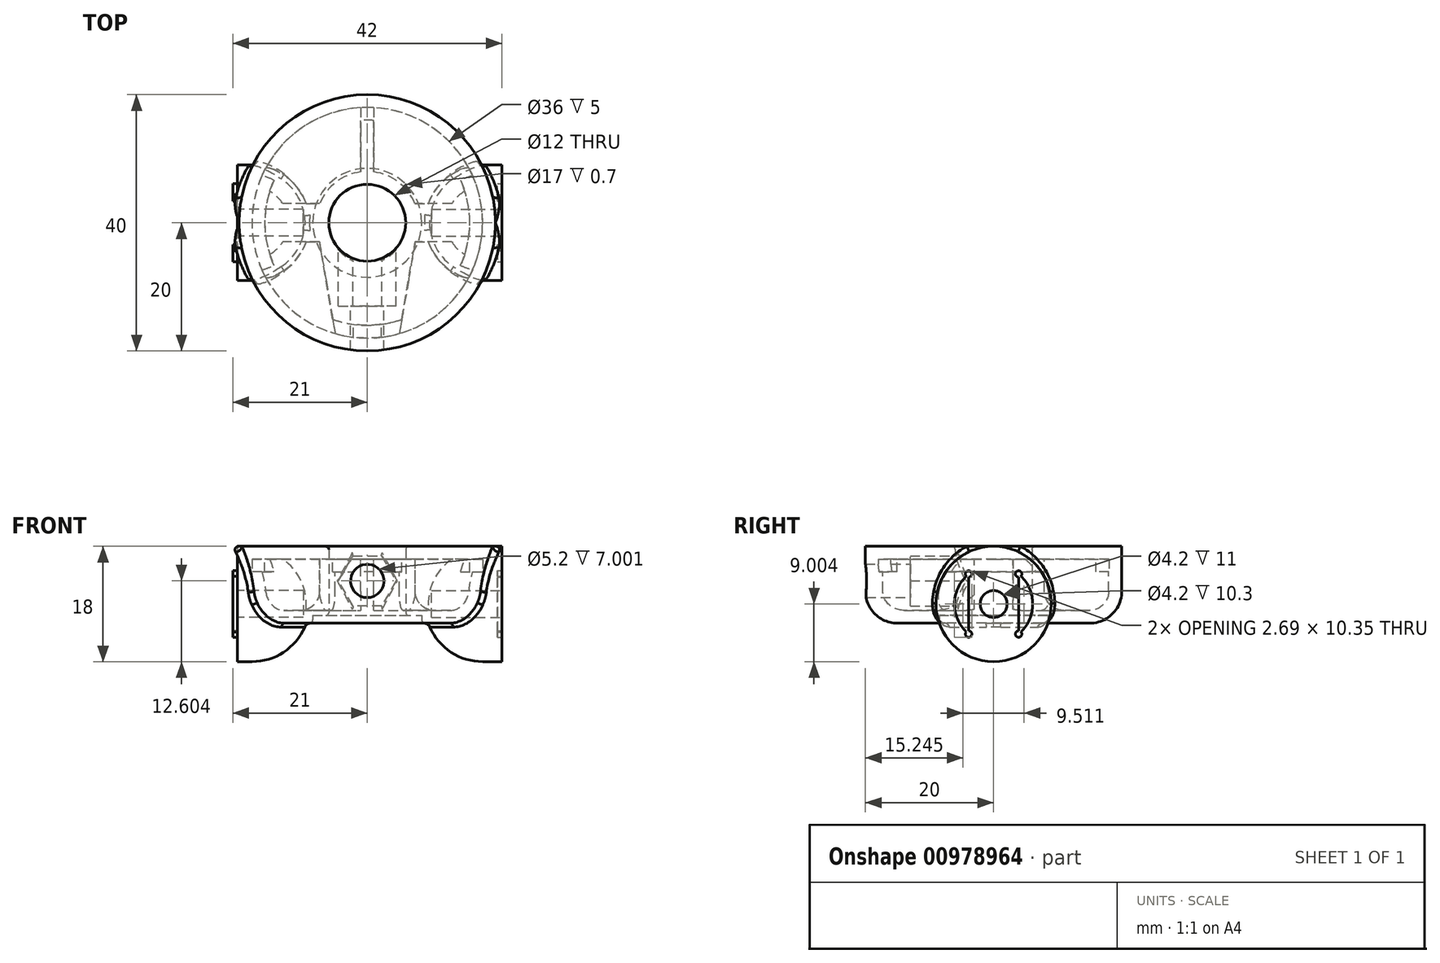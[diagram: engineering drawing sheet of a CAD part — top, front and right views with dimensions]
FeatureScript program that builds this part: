
annotation { "Feature Type Name" : "Feature", "Feature Type Description" : "" }
export const myFeature = defineFeature(function(context is Context, id is Id, definition is map)
    precondition{}
    {
        {
            var Q0;
            Q0=qCreatedBy(makeId("Front.planeOp"),FACE);
            var sketch = newSketch(context, id + "F0", { "sketchPlane" : qUnion([Q0])});
            skLineSegment(sketch, "E0", {"start": v(0, 0) * mm, "end": v(0, 29.29) * mm, "construction": true});
            skLineSegment(sketch, "E1", {"start": v(-6, 15.66) * mm, "end": v(-6, 4.86) * mm});
            skLineSegment(sketch, "E2", {"start": v(-6, 4.86) * mm, "end": v(-8.5, 4.86) * mm});
            skLineSegment(sketch, "E3", {"start": v(-8.5, 4.86) * mm, "end": v(-8.5, 3.66) * mm});
            skLineSegment(sketch, "E4", {"start": v(-8.5, 3.66) * mm, "end": v(-8.5, 3.66) * mm});
            skLineSegment(sketch, "E5", {"start": v(-8.5, 3.66) * mm, "end": v(-15, 3.66) * mm});
            skLineSegment(sketch, "E6", {"start": v(-20, 8.66) * mm, "end": v(-20, 15.66) * mm});
            skLineSegment(sketch, "E7", {"start": v(-20, 15.66) * mm, "end": v(-18, 15.66) * mm});
            skLineSegment(sketch, "E8", {"start": v(-18, 15.66) * mm, "end": v(-18, 15.66) * mm});
            skLineSegment(sketch, "E9", {"start": v(-18, 15.66) * mm, "end": v(-18, 8.66) * mm});
            skLineSegment(sketch, "E10", {"start": v(-15, 5.66) * mm, "end": v(-11, 5.66) * mm});
            skLineSegment(sketch, "E11", {"start": v(-8, 5.66) * mm, "end": v(-8, 5.66) * mm});
            skLineSegment(sketch, "E12", {"start": v(-8, 8.66) * mm, "end": v(-8, 15.66) * mm});
            skLineSegment(sketch, "E13", {"start": v(-6, 15.66) * mm, "end": v(-8, 15.66) * mm});
            skPoint(sketch, "E14.visualSharp", {"position": v(-20, 3.66) * mm});
            skArc(sketch, "E14.filletArc", {"start": v(-20, 8.66) * mm, "mid": v(-18.54, 5.13) * mm, "end": v(-15, 3.66) * mm});
            skPoint(sketch, "E15.visualSharp", {"position": v(-18, 5.66) * mm});
            skArc(sketch, "E15.filletArc", {"start": v(-18, 8.66) * mm, "mid": v(-17.12, 6.54) * mm, "end": v(-15, 5.66) * mm});
            skPoint(sketch, "E16.visualSharp", {"position": v(-8, 5.66) * mm});
            skArc(sketch, "E16.filletArc", {"start": v(-11, 5.66) * mm, "mid": v(-8.88, 6.54) * mm, "end": v(-8, 8.66) * mm});
            skSolve(sketch);
        }
        {
            var Q0;
            Q0=makeQuery(id+"F0.imprint","IMPRINT",FACE,{"disambiguationData":[TD([[makeQuery(id+"F0.imprint","IMPRINT",EDGE,{"derivedFrom":sQuery(id+"F0.wireOp",EDGE,"E1")}),-1.0]])]});
            var Q1;
            Q1=sQuery(id+"F0.wireOp",EDGE,"E0");
            revolve(context, id + "F1", {"surfaceOperationType" : NewSurfaceOperationType.NEW, "entities" : qUnion([Q0]), "axis" : qUnion([Q1]), "revolveType" : RevolveType.FULL});
        }
        {
            var Q0;
            Q0=makeQuery(id+"F1.opRevolve","SWEPT_FACE",FACE,{"disambiguationData":[OSD([sQuery(id+"F0.wireOp",EDGE,"E7")])]});
            cPlane(context, id + "F2", {"entities" : qUnion([Q0]), "cplaneType" : CPlaneType.OFFSET, "offset" : 9 * mm, "oppositeDirection" : true, "width" : 150 * mm, "height" : 150 * mm});
        }
        {
            var Q0;
            Q0=qCreatedBy(id+"F2.planeOp",FACE);
            var sketch = newSketch(context, id + "F3", { "sketchPlane" : qUnion([Q0])});
            skLineSegment(sketch, "E17.bottom", {"start": v(-9, 0) * mm, "end": v(-21, 0) * mm});
            skLineSegment(sketch, "E17.top", {"start": v(-18, -9) * mm, "end": v(-21, -9) * mm});
            skLineSegment(sketch, "E17.left", {"start": v(-9, 0) * mm, "end": v(-9, 0) * mm});
            skLineSegment(sketch, "E17.right", {"start": v(-21, 0) * mm, "end": v(-21, -9) * mm});
            skLineSegment(sketch, "E18.bottom", {"start": v(9, 0) * mm, "end": v(21, 0) * mm});
            skLineSegment(sketch, "E18.top", {"start": v(18, -9) * mm, "end": v(21, -9) * mm});
            skLineSegment(sketch, "E18.left", {"start": v(9, 0) * mm, "end": v(9, 0) * mm});
            skLineSegment(sketch, "E18.right", {"start": v(21, 0) * mm, "end": v(21, -9) * mm});
            skPoint(sketch, "E19.visualSharp", {"position": v(-9, -9) * mm});
            skArc(sketch, "E19.filletArc", {"start": v(-18, -9) * mm, "mid": v(-11.64, -6.36) * mm, "end": v(-9, 0) * mm});
            skPoint(sketch, "E20.visualSharp", {"position": v(9, -9) * mm});
            skArc(sketch, "E20.filletArc", {"start": v(9, 0) * mm, "mid": v(11.64, -6.36) * mm, "end": v(18, -9) * mm});
            skSolve(sketch);
        }
        {
            var Q0;
            Q0=makeQuery(id+"F3.imprint","IMPRINT",FACE,{"disambiguationData":[TD([[makeQuery(id+"F3.imprint","IMPRINT",EDGE,{"derivedFrom":sQuery(id+"F3.wireOp",EDGE,"E17.bottom")}),1.0]])]});
            var Q1;
            Q1=makeQuery(id+"F3.imprint","IMPRINT",FACE,{"disambiguationData":[TD([[makeQuery(id+"F3.imprint","IMPRINT",EDGE,{"derivedFrom":sQuery(id+"F3.wireOp",EDGE,"E18.bottom")}),-1.0]])]});
            var Q2;
            Q2=sQuery(id+"F3.wireOp",EDGE,"E17.bottom");
            revolve(context, id + "F4", {"operationType" : NewBodyOperationType.ADD, "surfaceOperationType" : NewSurfaceOperationType.NEW, "entities" : qUnion([Q0, Q1]), "axis" : qUnion([Q2]), "revolveType" : RevolveType.FULL});
        }
        {
            var Q0;
            Q0=makeQuery(id+"F1.opRevolve","SWEPT_FACE",FACE,{"disambiguationData":[OSD([sQuery(id+"F0.wireOp",EDGE,"E7")])]});
            var sketch = newSketch(context, id + "F5", { "sketchPlane" : qUnion([Q0])});
            skLineSegment(sketch, "E21.bottom", {"start": v(-19.77, 3) * mm, "end": v(19.77, 3) * mm});
            skLineSegment(sketch, "E21.top", {"start": v(-19.77, -3) * mm, "end": v(19.77, -3) * mm});
            skLineSegment(sketch, "E21.left", {"start": v(-19.77, 3) * mm, "end": v(-19.77, -3) * mm});
            skLineSegment(sketch, "E21.right", {"start": v(19.77, 3) * mm, "end": v(19.77, -3) * mm});
            skLineSegment(sketch, "E22", {"start": v(-7, 3) * mm, "end": v(-7, -3) * mm});
            skLineSegment(sketch, "E23", {"start": v(7, 3) * mm, "end": v(7, -3) * mm});
            skSolve(sketch);
        }
        {
            var Q0;
            {var subQ0=sQuery(id+"F5.wireOp",EDGE,"E23");Q0=makeQuery(id+"F5.imprint","IMPRINT",FACE,{"disambiguationData":[TD([[makeQuery(id+"F5.imprint","IMPRINT",EDGE,{"derivedFrom":subQ0}),1.0]])]});}
            var Q1;
            {var subQ0=sQuery(id+"F5.wireOp",EDGE,"E22");Q1=makeQuery(id+"F5.imprint","IMPRINT",FACE,{"disambiguationData":[TD([[makeQuery(id+"F5.imprint","IMPRINT",EDGE,{"derivedFrom":subQ0}),-1.0]])]});}
            extrude(context, id + "F6", {"entities" : qUnion([Q0, Q1]), "operationType" : NewBodyOperationType.ADD, "oppositeDirection" : true, "depth" : 10 * mm, "offsetDistance" : 25 * mm});
        }
        {
            var Q0;
            Q0=makeQuery(id+"F4.opRevolve","SWEPT_FACE",FACE,{"disambiguationData":[OSD([sQuery(id+"F3.wireOp",EDGE,"E18.right")])]});
            var sketch = newSketch(context, id + "F7", { "sketchPlane" : qUnion([Q0])});
            skCircle(sketch, "E24.0", {"center": v(0, 6.66) * mm, "radius": 9 * mm});
            skCircle(sketch, "E25", {"center": v(0, 6.66) * mm, "radius": 2.1 * mm});
            skSolve(sketch);
        }
        {
            var Q0;
            Q0=makeQuery(id+"F7.imprint","IMPRINT",FACE,{"disambiguationData":[TD([[makeQuery(id+"F7.imprint","IMPRINT",EDGE,{"derivedFrom":sQuery(id+"F7.wireOp",EDGE,"E25")}),1.0]])]});
            extrude(context, id + "F8", {"entities" : qUnion([Q0]), "operationType" : NewBodyOperationType.REMOVE, "oppositeDirection" : true, "depth" : 11 * mm, "offsetDistance" : 25 * mm});
        }
        {
            var Q0;
            Q0=makeQuery(id+"F4.opRevolve","SWEPT_FACE",FACE,{"disambiguationData":[OSD([sQuery(id+"F3.wireOp",EDGE,"E17.right")])]});
            var sketch = newSketch(context, id + "F9", { "sketchPlane" : qUnion([Q0])});
            skCircle(sketch, "E26.0", {"center": v(0, 6.66) * mm, "radius": 2.1 * mm});
            skSolve(sketch);
        }
        {
            var Q0;
            Q0=makeQuery(id+"F9.imprint","IMPRINT",FACE,{"disambiguationData":[TD([[makeQuery(id+"F9.imprint","IMPRINT",EDGE,{"derivedFrom":sQuery(id+"F9.wireOp",EDGE,"E26.0")}),1.0]])]});
            extrude(context, id + "F10", {"entities" : qUnion([Q0]), "operationType" : NewBodyOperationType.REMOVE, "oppositeDirection" : true, "depth" : 11 * mm, "offsetDistance" : 25 * mm});
        }
        {
            var Q0;
            {var subQ0=sQuery(id+"F5.wireOp",EDGE,"E21.top");var subQ1=sQuery(id+"F5.wireOp",EDGE,"E21.bottom");var subQ2=sQuery(id+"F0.wireOp",EDGE,"E9");var subQ3=sQuery(id+"F0.wireOp",EDGE,"E7");Q0=makeQuery(id+"F6.boolean.opBoolean","MERGE",FACE,{"derivedFrom":[makeQuery(id+"F1.opRevolve","SWEPT_FACE",FACE,{"disambiguationData":[OSD([subQ3])]}),makeQuery(id+"F1.opRevolve","SWEPT_FACE",FACE,{"disambiguationData":[OSD([sQuery(id+"F0.wireOp",EDGE,"E13")])]}),makeQuery(id+"F6.opExtrude","CAP_FACE",FACE,{"disambiguationData":[OSD([subQ3,subQ2,subQ1,subQ0,sQuery(id+"F5.wireOp",EDGE,"E22")])],"isStart":true}),makeQuery(id+"F6.opExtrude","CAP_FACE",FACE,{"disambiguationData":[OSD([subQ3,subQ2,subQ1,subQ0,sQuery(id+"F5.wireOp",EDGE,"E23")])],"isStart":true})]});}
            var sketch = newSketch(context, id + "F11", { "sketchPlane" : qUnion([Q0])});
            skLineSegment(sketch, "E27", {"start": v(-7.5, -2.78) * mm, "end": v(-5, -17.3) * mm});
            skLineSegment(sketch, "E28", {"start": v(7.5, -2.78) * mm, "end": v(5, -17.3) * mm});
            skSolve(sketch);
        }
        {
            var Q0;
            {var subQ0=sQuery(id+"F11.wireOp",EDGE,"E27");Q0=makeQuery(id+"F11.imprint","IMPRINT",FACE,{"disambiguationData":[TD([[makeQuery(id+"F11.imprint","IMPRINT",EDGE,{"derivedFrom":subQ0}),1.0]])]});}
            extrude(context, id + "F12", {"entities" : qUnion([Q0]), "operationType" : NewBodyOperationType.ADD, "oppositeDirection" : true, "depth" : 10 * mm, "offsetDistance" : 25 * mm});
        }
        {
            var Q0;
            Q0=qCreatedBy(makeId("Front.planeOp"),FACE);
            var sketch = newSketch(context, id + "F13", { "sketchPlane" : qUnion([Q0])});
            skCircle(sketch, "E29", {"center": v(0, 10.26) * mm, "radius": 2.6 * mm});
            skSolve(sketch);
        }
        {
            var Q0;
            Q0=qSketchRegion(id+"F13",true);
            extrude(context, id + "F14", {"entities" : qUnion([Q0]), "operationType" : NewBodyOperationType.REMOVE, "depth" : 25 * mm, "offsetDistance" : 25 * mm});
        }
        {
            var Q0;
            {var subQ0=sQuery(id+"F0.wireOp",EDGE,"E13");var subQ1=sQuery(id+"F0.wireOp",EDGE,"E9");var subQ2=sQuery(id+"F0.wireOp",EDGE,"E7");var subQ3=sQuery(id+"F5.wireOp",EDGE,"E21.top");var subQ4=sQuery(id+"F5.wireOp",EDGE,"E21.bottom");Q0=makeQuery(id+"F12.boolean.opBoolean","MERGE",FACE,{"derivedFrom":[makeQuery(id+"F6.boolean.opBoolean","MERGE",FACE,{"derivedFrom":[makeQuery(id+"F1.opRevolve","SWEPT_FACE",FACE,{"disambiguationData":[OSD([subQ2])]}),makeQuery(id+"F1.opRevolve","SWEPT_FACE",FACE,{"disambiguationData":[OSD([subQ0])]}),makeQuery(id+"F6.opExtrude","CAP_FACE",FACE,{"disambiguationData":[OSD([subQ2,subQ1,subQ4,subQ3,sQuery(id+"F5.wireOp",EDGE,"E22")])],"isStart":true}),makeQuery(id+"F6.opExtrude","CAP_FACE",FACE,{"disambiguationData":[OSD([subQ2,subQ1,subQ4,subQ3,sQuery(id+"F5.wireOp",EDGE,"E23")])],"isStart":true})]}),makeQuery(id+"F12.opExtrude","CAP_FACE",FACE,{"disambiguationData":[OSD([subQ2,subQ1,sQuery(id+"F0.wireOp",EDGE,"E12"),subQ0,sQuery(id+"F11.wireOp",EDGE,"E27"),sQuery(id+"F11.wireOp",EDGE,"E28")])],"isStart":true})]});}
            var sketch = newSketch(context, id + "F15", { "sketchPlane" : qUnion([Q0])});
            skLineSegment(sketch, "E30.bottom", {"start": v(-1, 18.3) * mm, "end": v(1, 18.3) * mm});
            skLineSegment(sketch, "E30.top", {"start": v(-1, 7.14) * mm, "end": v(1, 7.14) * mm});
            skLineSegment(sketch, "E30.left", {"start": v(-1, 18.3) * mm, "end": v(-1, 7.14) * mm});
            skLineSegment(sketch, "E30.right", {"start": v(1, 18.3) * mm, "end": v(1, 7.14) * mm});
            skSolve(sketch);
        }
        {
            var Q0;
            {var subQ0=sQuery(id+"F15.wireOp",EDGE,"E30.left");var subQ1=sQuery(id+"F5.wireOp",EDGE,"E22");var subQ2=sQuery(id+"F5.wireOp",EDGE,"E21.bottom");var subQ3=sQuery(id+"F0.wireOp",EDGE,"E9");var subQ4=sQuery(id+"F0.wireOp",EDGE,"E7");var subQ5=makeQuery(id+"F1.opRevolve","SWEPT_EDGE",EDGE,{"disambiguationData":[OSD([subQ4,subQ3])]});var subQ6=makeQuery(id+"F6.opExtrude","SWEPT_FACE",FACE,{"disambiguationData":[OSD([subQ2]),TDD([makeQuery(id+"F5.imprint","IMPRINT",EDGE,{"disambiguationData":[TD([[makeQuery(id+"F5.imprint","INTERSECT",VERTEX,{"derivedFrom":[subQ2,subQ1]}),1.0]])],"derivedFrom":subQ2})])]});var subQ15=makeQuery(id+"F6.boolean.opBoolean","SPLIT",EDGE,{"disambiguationData":[TD([subQ6])],"derivedFrom":subQ5});var subQ16=makeQuery(id+"F15.imprint","INTERSECT",VERTEX,{"derivedFrom":[subQ15,subQ0]});Q0=makeQuery(id+"F15.imprint","IMPRINT",FACE,{"disambiguationData":[TD([[makeQuery(id+"F15.imprint","IMPRINT",EDGE,{"disambiguationData":[TD([[subQ16,-1.0]])],"derivedFrom":subQ0}),1.0]])]});}
            extrude(context, id + "F16", {"entities" : qUnion([Q0]), "operationType" : NewBodyOperationType.ADD, "oppositeDirection" : true, "depth" : 10 * mm, "offsetDistance" : 25 * mm});
        }
        {
            var Q0;
            Q0=makeQuery(id+"F1.opRevolve","SWEPT_EDGE",EDGE,{"disambiguationData":[OSD([sQuery(id+"F0.wireOp",EDGE,"E1"),sQuery(id+"F0.wireOp",EDGE,"E2")])]});
            var Q1;
            Q1=makeQuery(id+"F1.opRevolve","SWEPT_EDGE",EDGE,{"disambiguationData":[OSD([sQuery(id+"F0.wireOp",EDGE,"E3"),sQuery(id+"F0.wireOp",EDGE,"E5")])]});
            var Q2;
            Q2=makeQuery(id+"F1.opRevolve","SWEPT_EDGE",EDGE,{"disambiguationData":[OSD([sQuery(id+"F0.wireOp",EDGE,"E1"),sQuery(id+"F0.wireOp",EDGE,"E13")])]});
            var Q3;
            Q3=makeQuery(id+"F28.boolean.opBoolean","INTERSECT",EDGE,{"derivedFrom":[makeQuery(id+"F1.opRevolve","SWEPT_FACE",FACE,{"disambiguationData":[OSD([sQuery(id+"F0.wireOp",EDGE,"E1")])]}),makeQuery(id+"F28.opExtrude","SWEPT_FACE",FACE,{"disambiguationData":[OSD([sQuery(id+"F27.wireOp",EDGE,"E51.5")])]})]});
            var Q4;
            Q4=makeQuery(id+"F28.boolean.opBoolean","INTERSECT",EDGE,{"derivedFrom":[makeQuery(id+"F1.opRevolve","SWEPT_FACE",FACE,{"disambiguationData":[OSD([sQuery(id+"F0.wireOp",EDGE,"E1")])]}),makeQuery(id+"F28.opExtrude","SWEPT_FACE",FACE,{"disambiguationData":[OSD([sQuery(id+"F27.wireOp",EDGE,"E51.4")])]})]});
            var Q5;
            Q5=makeQuery(id+"F28.boolean.opBoolean","INTERSECT",EDGE,{"derivedFrom":[makeQuery(id+"F1.opRevolve","SWEPT_FACE",FACE,{"disambiguationData":[OSD([sQuery(id+"F0.wireOp",EDGE,"E1")])]}),makeQuery(id+"F28.opExtrude","SWEPT_FACE",FACE,{"disambiguationData":[OSD([sQuery(id+"F27.wireOp",EDGE,"E51.3")])]})]});
            var Q6;
            Q6=makeQuery(id+"F28.boolean.opBoolean","INTERSECT",EDGE,{"derivedFrom":[makeQuery(id+"F1.opRevolve","SWEPT_FACE",FACE,{"disambiguationData":[OSD([sQuery(id+"F0.wireOp",EDGE,"E1")])]}),makeQuery(id+"F28.opExtrude","SWEPT_FACE",FACE,{"disambiguationData":[OSD([sQuery(id+"F27.wireOp",EDGE,"E51.2")])]})]});
            var Q7;
            Q7=makeQuery(id+"F28.boolean.opBoolean","INTERSECT",EDGE,{"derivedFrom":[makeQuery(id+"F1.opRevolve","SWEPT_FACE",FACE,{"disambiguationData":[OSD([sQuery(id+"F0.wireOp",EDGE,"E1")])]}),makeQuery(id+"F28.opExtrude","SWEPT_FACE",FACE,{"disambiguationData":[OSD([sQuery(id+"F27.wireOp",EDGE,"E51.1")])]})]});
            var Q8;
            Q8=makeQuery(id+"F28.boolean.opBoolean","INTERSECT",EDGE,{"derivedFrom":[makeQuery(id+"F1.opRevolve","SWEPT_FACE",FACE,{"disambiguationData":[OSD([sQuery(id+"F0.wireOp",EDGE,"E1")])]}),makeQuery(id+"F28.opExtrude","SWEPT_FACE",FACE,{"disambiguationData":[OSD([sQuery(id+"F27.wireOp",EDGE,"E51.0")])]})]});
            fillet(context, id + "F17", {"entities" : qUnion([Q0, Q1, Q2, Q3, Q4, Q5, Q6, Q7, Q8]), "radius" : 0.5 * mm, "tangentPropagation" : true, "allowEdgeOverflow" : false});
        }
        {
            var Q0;
            Q0=qCreatedBy(makeId("Right.planeOp"),FACE);
            var sketch = newSketch(context, id + "F18", { "sketchPlane" : qUnion([Q0])});
            skLineSegment(sketch, "E31.bottom", {"start": v(18, 18.33) * mm, "end": v(16, 18.33) * mm});
            skLineSegment(sketch, "E31.top", {"start": v(18, 11.66) * mm, "end": v(16, 11.66) * mm});
            skLineSegment(sketch, "E31.left", {"start": v(18, 18.33) * mm, "end": v(18, 11.66) * mm});
            skLineSegment(sketch, "E31.right", {"start": v(16, 18.33) * mm, "end": v(16, 11.66) * mm});
            skLineSegment(sketch, "E32", {"start": v(0, 0) * mm, "end": v(0, 18.33) * mm, "construction": true});
            skSolve(sketch);
        }
        {
            var Q0;
            Q0=makeQuery(id+"F18.imprint","IMPRINT",FACE,{"disambiguationData":[TD([[makeQuery(id+"F18.imprint","IMPRINT",EDGE,{"derivedFrom":sQuery(id+"F18.wireOp",EDGE,"E31.bottom")}),1.0]])]});
            var Q1;
            Q1=sQuery(id+"F18.wireOp",EDGE,"E32");
            revolve(context, id + "F19", {"operationType" : NewBodyOperationType.REMOVE, "surfaceOperationType" : NewSurfaceOperationType.NEW, "entities" : qUnion([Q0]), "axis" : qUnion([Q1]), "revolveType" : RevolveType.FULL, "oppositeDirection" : true});
        }
        {
            var Q0;
            Q0=makeQuery(id+"F4.boolean.opBoolean","INTERSECT",EDGE,{"derivedFrom":[makeQuery(id+"F1.opRevolve","SWEPT_FACE",FACE,{"disambiguationData":[OSD([sQuery(id+"F0.wireOp",EDGE,"E5")])]}),makeQuery(id+"F4.opRevolve","SWEPT_FACE",FACE,{"disambiguationData":[OSD([sQuery(id+"F3.wireOp",EDGE,"E20.filletArc")])]})]});
            var Q1;
            Q1=makeQuery(id+"F4.boolean.opBoolean","INTERSECT",EDGE,{"derivedFrom":[makeQuery(id+"F1.opRevolve","SWEPT_FACE",FACE,{"disambiguationData":[OSD([sQuery(id+"F0.wireOp",EDGE,"E5")])]}),makeQuery(id+"F4.opRevolve","SWEPT_FACE",FACE,{"disambiguationData":[OSD([sQuery(id+"F3.wireOp",EDGE,"E19.filletArc")])]})]});
            fillet(context, id + "F20", {"entities" : qUnion([Q0, Q1]), "radius" : 1 * mm, "tangentPropagation" : true, "allowEdgeOverflow" : false});
        }
        {
            var Q0;
            {var subQ2=sQuery(id+"F0.wireOp",EDGE,"E6");var subQ3=makeQuery(id+"F1.opRevolve","SWEPT_FACE",FACE,{"disambiguationData":[OSD([subQ2])]});var subQ6=sQuery(id+"F0.wireOp",EDGE,"E9");var subQ11=sQuery(id+"F0.wireOp",EDGE,"E13");var subQ12=sQuery(id+"F0.wireOp",EDGE,"E12");var subQ13=sQuery(id+"F0.wireOp",EDGE,"E7");var subQ14=sQuery(id+"F5.wireOp",EDGE,"E21.top");var subQ15=sQuery(id+"F5.wireOp",EDGE,"E21.bottom");Q0=makeQuery(id+"F19.boolean.opBoolean","SPLIT",FACE,{"disambiguationData":[TD([subQ3])],"derivedFrom":makeQuery(id+"F16.boolean.opBoolean","MERGE",FACE,{"derivedFrom":[makeQuery(id+"F12.boolean.opBoolean","MERGE",FACE,{"derivedFrom":[makeQuery(id+"F6.boolean.opBoolean","MERGE",FACE,{"derivedFrom":[makeQuery(id+"F1.opRevolve","SWEPT_FACE",FACE,{"disambiguationData":[OSD([subQ13])]}),makeQuery(id+"F1.opRevolve","SWEPT_FACE",FACE,{"disambiguationData":[OSD([subQ11])]}),makeQuery(id+"F6.opExtrude","CAP_FACE",FACE,{"disambiguationData":[OSD([subQ13,subQ6,subQ15,subQ14,sQuery(id+"F5.wireOp",EDGE,"E22")])],"isStart":true}),makeQuery(id+"F6.opExtrude","CAP_FACE",FACE,{"disambiguationData":[OSD([subQ13,subQ6,subQ15,subQ14,sQuery(id+"F5.wireOp",EDGE,"E23")])],"isStart":true})]}),makeQuery(id+"F12.opExtrude","CAP_FACE",FACE,{"disambiguationData":[OSD([subQ13,subQ6,subQ12,subQ11,subQ14,sQuery(id+"F11.wireOp",EDGE,"E27"),sQuery(id+"F11.wireOp",EDGE,"E28")])],"isStart":true})]}),makeQuery(id+"F16.opExtrude","CAP_FACE",FACE,{"disambiguationData":[OSD([subQ13,subQ6,subQ12,subQ11,sQuery(id+"F15.wireOp",EDGE,"E30.left"),sQuery(id+"F15.wireOp",EDGE,"E30.right")])],"isStart":true})]})});}
            var sketch = newSketch(context, id + "F21", { "sketchPlane" : qUnion([Q0])});
            skCircle(sketch, "E33", {"center": v(0, 0) * mm, "radius": 20 * mm});
            skCircle(sketch, "E34", {"center": v(0, 0) * mm, "radius": 7 * mm});
            skSolve(sketch);
        }
        {
            var Q0;
            {var subQ0=sQuery(id+"F21.wireOp",EDGE,"E33");var subQ5=makeQuery(id+"F21.imprint","IMPRINT",VERTEX,{"disambiguationData":[OD(0.0)],"derivedFrom":subQ0});Q0=makeQuery(id+"F21.imprint","IMPRINT",FACE,{"disambiguationData":[TD([[makeQuery(id+"F21.imprint","IMPRINT",EDGE,{"disambiguationData":[TD([[subQ5,-1.0]])],"derivedFrom":subQ0}),-1.0]])]});}
            var Q1;
            Q1=makeQuery(id+"F21.imprint","IMPRINT",FACE,{"disambiguationData":[TD([[makeQuery(id+"F21.imprint","IMPRINT",EDGE,{"derivedFrom":sQuery(id+"F21.wireOp",EDGE,"E34")}),-1.0]])]});
            extrude(context, id + "F22", {"entities" : qUnion([Q0, Q1]), "operationType" : NewBodyOperationType.ADD, "oppositeDirection" : true, "depth" : 2 * mm, "offsetDistance" : 25 * mm});
        }
        {
            var Q0;
            Q0=makeQuery(id+"F4.opRevolve","SWEPT_FACE",FACE,{"disambiguationData":[OSD([sQuery(id+"F3.wireOp",EDGE,"E18.right")])]});
            var sketch = newSketch(context, id + "F23", { "sketchPlane" : qUnion([Q0])});
            skCircle(sketch, "E35.0", {"center": v(0, 6.66) * mm, "radius": 2.1 * mm});
            skArc(sketch, "E36", {"start": v(-4.27, 11.02) * mm, "mid": v(-6.1, 6.66) * mm, "end": v(-4.27, 2.3) * mm, "construction": true});
            skLineSegment(sketch, "E37", {"start": v(-3.9, 10.85) * mm, "end": v(-3.9, 2.47) * mm});
            skLineSegment(sketch, "E38", {"start": v(3.9, 10.85) * mm, "end": v(3.9, 2.47) * mm});
            skArc(sketch, "E39", {"start": v(-3.9, 10.85) * mm, "mid": v(-3.7, 11.81) * mm, "end": v(-4.27, 11.02) * mm});
            skArc(sketch, "E40", {"start": v(4.27, 11.02) * mm, "mid": v(3.7, 11.81) * mm, "end": v(3.9, 10.85) * mm});
            skArc(sketch, "E41", {"start": v(3.9, 2.47) * mm, "mid": v(3.7, 1.52) * mm, "end": v(4.27, 2.3) * mm});
            skArc(sketch, "E42", {"start": v(-4.27, 2.3) * mm, "mid": v(-3.7, 1.52) * mm, "end": v(-3.9, 2.47) * mm});
            skArc(sketch, "E43", {"start": v(-4.27, 11.02) * mm, "mid": v(-6.1, 6.66) * mm, "end": v(-4.27, 2.3) * mm});
            skArc(sketch, "E44", {"start": v(4.27, 11.02) * mm, "mid": v(6.1, 6.66) * mm, "end": v(4.27, 2.3) * mm});
            skArc(sketch, "E45.trimOffspring", {"start": v(3.5, 11.66) * mm, "mid": v(0, 12.76) * mm, "end": v(-3.5, 11.66) * mm, "construction": true});
            skArc(sketch, "E46.trimOffspring", {"start": v(4.27, 2.3) * mm, "mid": v(6.1, 6.66) * mm, "end": v(4.27, 11.02) * mm, "construction": true});
            skArc(sketch, "E47.trimOffspring", {"start": v(-3.9, 1.97) * mm, "mid": v(-0.25, 0.57) * mm, "end": v(3.5, 1.67) * mm, "construction": true});
            skSolve(sketch);
        }
        {
            var Q0;
            Q0=makeQuery(id+"F23.imprint","IMPRINT",FACE,{"disambiguationData":[TD([[makeQuery(id+"F23.imprint","IMPRINT",EDGE,{"derivedFrom":sQuery(id+"F23.wireOp",EDGE,"E37")}),-1.0]])]});
            var Q1;
            Q1=makeQuery(id+"F23.imprint","IMPRINT",FACE,{"disambiguationData":[TD([[makeQuery(id+"F23.imprint","IMPRINT",EDGE,{"derivedFrom":sQuery(id+"F23.wireOp",EDGE,"E38")}),1.0]])]});
            extrude(context, id + "F24", {"entities" : qUnion([Q0, Q1]), "operationType" : NewBodyOperationType.REMOVE, "oppositeDirection" : true, "depth" : .7 * mm, "offsetDistance" : 25 * mm});
        }
        {
            var Q0;
            Q0=makeQuery(id+"F4.opRevolve","SWEPT_FACE",FACE,{"disambiguationData":[OSD([sQuery(id+"F3.wireOp",EDGE,"E17.right")])]});
            var sketch = newSketch(context, id + "F25", { "sketchPlane" : qUnion([Q0])});
            skArc(sketch, "E48.0.0", {"start": v(-4.27, 2.3) * mm, "mid": v(-6.1, 6.66) * mm, "end": v(-4.27, 11.02) * mm});
            skArc(sketch, "E48.0.1", {"start": v(-4.27, 11.02) * mm, "mid": v(-3.7, 11.81) * mm, "end": v(-3.9, 10.85) * mm});
            skLineSegment(sketch, "E48.0.2", {"start": v(-3.9, 10.85) * mm, "end": v(-3.9, 2.47) * mm});
            skArc(sketch, "E48.0.3", {"start": v(-3.9, 2.47) * mm, "mid": v(-3.7, 1.52) * mm, "end": v(-4.27, 2.3) * mm});
            skArc(sketch, "E49.0.0", {"start": v(3.9, 10.85) * mm, "mid": v(3.7, 11.81) * mm, "end": v(4.27, 11.02) * mm});
            skArc(sketch, "E49.0.1", {"start": v(4.27, 11.02) * mm, "mid": v(6.1, 6.66) * mm, "end": v(4.27, 2.3) * mm});
            skArc(sketch, "E49.0.2", {"start": v(4.27, 2.3) * mm, "mid": v(3.7, 1.52) * mm, "end": v(3.9, 2.47) * mm});
            skLineSegment(sketch, "E49.0.3", {"start": v(3.9, 2.47) * mm, "end": v(3.9, 10.85) * mm});
            skSolve(sketch);
        }
        {
            var Q0;
            Q0=makeQuery(id+"F25.imprint","IMPRINT",FACE,{"disambiguationData":[TD([[makeQuery(id+"F25.imprint","IMPRINT",EDGE,{"derivedFrom":sQuery(id+"F25.wireOp",EDGE,"E49.0.0")}),-1.0]])]});
            var Q1;
            Q1=makeQuery(id+"F25.imprint","IMPRINT",FACE,{"disambiguationData":[TD([[makeQuery(id+"F25.imprint","IMPRINT",EDGE,{"derivedFrom":sQuery(id+"F25.wireOp",EDGE,"E48.0.0")}),-1.0]])]});
            extrude(context, id + "F26", {"entities" : qUnion([Q0, Q1]), "operationType" : NewBodyOperationType.REMOVE, "oppositeDirection" : true, "depth" : .7 * mm, "offsetDistance" : 25 * mm});
        }
        {
            var Q0;
            Q0=qCreatedBy(makeId("Front.planeOp"),FACE);
            var sketch = newSketch(context, id + "F27", { "sketchPlane" : qUnion([Q0])});
            skArc(sketch, "E50.0", {"start": v(-2.05, 8.66) * mm, "mid": v(0, 12.86) * mm, "end": v(2.05, 8.66) * mm});
            skCircle(sketch, "E51.cCircle", {"center": v(0, 10.26) * mm, "radius": 3.9 * mm, "construction": true});
            skLineSegment(sketch, "E51.0", {"start": v(-2.25, 14.16) * mm, "end": v(2.25, 14.16) * mm});
            skLineSegment(sketch, "E51.1", {"start": v(2.25, 14.16) * mm, "end": v(4.5, 10.26) * mm});
            skLineSegment(sketch, "E51.2", {"start": v(4.5, 10.26) * mm, "end": v(2.25, 6.36) * mm});
            skLineSegment(sketch, "E51.3", {"start": v(2.25, 6.36) * mm, "end": v(-2.25, 6.36) * mm});
            skLineSegment(sketch, "E51.4", {"start": v(-2.25, 6.36) * mm, "end": v(-4.5, 10.26) * mm});
            skLineSegment(sketch, "E51.5", {"start": v(-4.5, 10.26) * mm, "end": v(-2.25, 14.16) * mm});
            skPoint(sketch, "E51.0.midPoint", {"position": v(0, 14.16) * mm});
            skSolve(sketch);
        }
        {
            var Q0;
            Q0=makeQuery(id+"F27.imprint","IMPRINT",FACE,{"disambiguationData":[TD([[makeQuery(id+"F27.imprint","IMPRINT",EDGE,{"derivedFrom":sQuery(id+"F27.wireOp",EDGE,"E51.0")}),-1.0]])]});
            extrude(context, id + "F28", {"entities" : qUnion([Q0]), "operationType" : NewBodyOperationType.REMOVE, "depth" : 13 * mm, "offsetDistance" : 25 * mm});
        }
        {
            var Q0;
            Q0=makeQuery(id+"F28.boolean.opBoolean","INTERSECT",EDGE,{"derivedFrom":[makeQuery(id+"F1.opRevolve","SWEPT_FACE",FACE,{"disambiguationData":[OSD([sQuery(id+"F0.wireOp",EDGE,"E1")])]}),makeQuery(id+"F28.opExtrude","SWEPT_FACE",FACE,{"disambiguationData":[OSD([sQuery(id+"F27.wireOp",EDGE,"E51.2")])]})]});
            var Q1;
            Q1=makeQuery(id+"F28.boolean.opBoolean","INTERSECT",EDGE,{"derivedFrom":[makeQuery(id+"F1.opRevolve","SWEPT_FACE",FACE,{"disambiguationData":[OSD([sQuery(id+"F0.wireOp",EDGE,"E1")])]}),makeQuery(id+"F28.opExtrude","SWEPT_FACE",FACE,{"disambiguationData":[OSD([sQuery(id+"F27.wireOp",EDGE,"E51.1")])]})]});
            var Q2;
            Q2=makeQuery(id+"F28.boolean.opBoolean","INTERSECT",EDGE,{"derivedFrom":[makeQuery(id+"F1.opRevolve","SWEPT_FACE",FACE,{"disambiguationData":[OSD([sQuery(id+"F0.wireOp",EDGE,"E1")])]}),makeQuery(id+"F28.opExtrude","SWEPT_FACE",FACE,{"disambiguationData":[OSD([sQuery(id+"F27.wireOp",EDGE,"E51.0")])]})]});
            var Q3;
            Q3=makeQuery(id+"F28.boolean.opBoolean","INTERSECT",EDGE,{"derivedFrom":[makeQuery(id+"F1.opRevolve","SWEPT_FACE",FACE,{"disambiguationData":[OSD([sQuery(id+"F0.wireOp",EDGE,"E1")])]}),makeQuery(id+"F28.opExtrude","SWEPT_FACE",FACE,{"disambiguationData":[OSD([sQuery(id+"F27.wireOp",EDGE,"E51.5")])]})]});
            var Q4;
            Q4=makeQuery(id+"F28.boolean.opBoolean","INTERSECT",EDGE,{"derivedFrom":[makeQuery(id+"F1.opRevolve","SWEPT_FACE",FACE,{"disambiguationData":[OSD([sQuery(id+"F0.wireOp",EDGE,"E1")])]}),makeQuery(id+"F28.opExtrude","SWEPT_FACE",FACE,{"disambiguationData":[OSD([sQuery(id+"F27.wireOp",EDGE,"E51.4")])]})]});
            var Q5;
            Q5=makeQuery(id+"F28.boolean.opBoolean","INTERSECT",EDGE,{"derivedFrom":[makeQuery(id+"F1.opRevolve","SWEPT_FACE",FACE,{"disambiguationData":[OSD([sQuery(id+"F0.wireOp",EDGE,"E1")])]}),makeQuery(id+"F28.opExtrude","SWEPT_FACE",FACE,{"disambiguationData":[OSD([sQuery(id+"F27.wireOp",EDGE,"E51.3")])]})]});
            fillet(context, id + "F29", {"entities" : qUnion([Q0, Q1, Q2, Q3, Q4, Q5]), "radius" : .5 * mm, "tangentPropagation" : true, "allowEdgeOverflow" : false});
        }
    });
